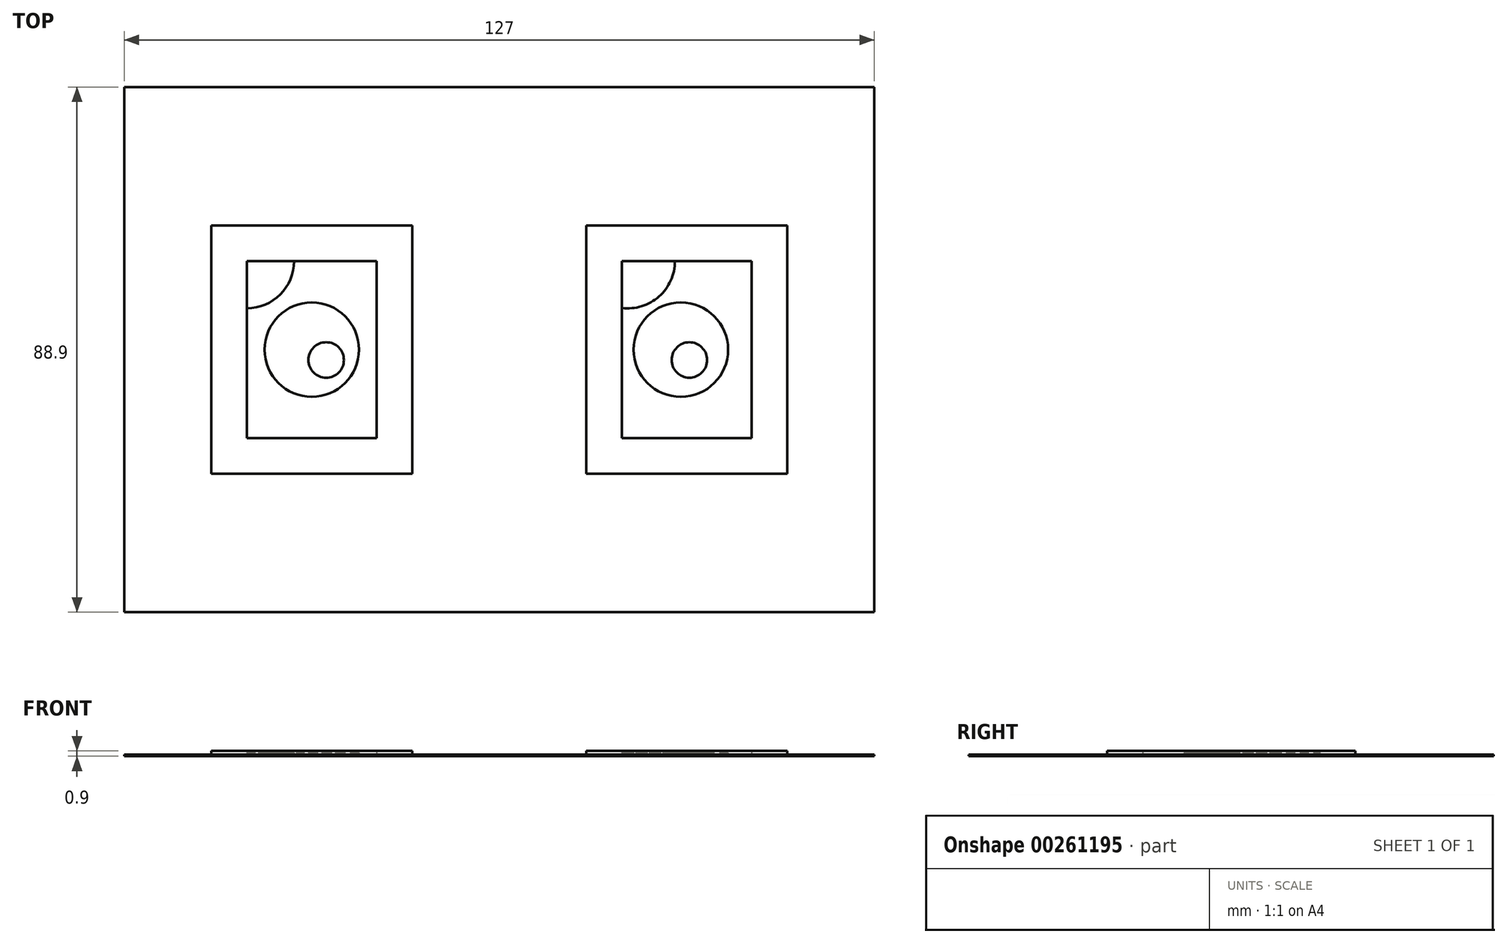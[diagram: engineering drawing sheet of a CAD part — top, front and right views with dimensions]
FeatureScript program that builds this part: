
annotation { "Feature Type Name" : "Feature", "Feature Type Description" : "" }
export const myFeature = defineFeature(function(context is Context, id is Id, definition is map)
    precondition{}
    {
        {
            var Q0;
            Q0=qCreatedBy(makeId("Top.planeOp"),FACE);
            var sketch = newSketch(context, id + "F0", { "sketchPlane" : qUnion([Q0])});
            skLineSegment(sketch, "E0.bottom", {"start": v(63.5, -44.45) * mm, "end": v(-63.5, -44.45) * mm});
            skLineSegment(sketch, "E0.top", {"start": v(63.5, 44.45) * mm, "end": v(-63.5, 44.45) * mm});
            skLineSegment(sketch, "E0.left", {"start": v(63.5, -44.45) * mm, "end": v(63.5, 44.45) * mm});
            skLineSegment(sketch, "E0.right", {"start": v(-63.5, -44.45) * mm, "end": v(-63.5, 44.45) * mm});
            skPoint(sketch, "E0.middle", {"position": v(0, 0) * mm});
            skSolve(sketch);
        }
        {
            var Q0;
            Q0 = qSketchRegion(id + "F0", true);
            extrude(context, id + "F1", {"entities" : qUnion([Q0]), "depth" : .3 * mm});
        }
        {
            var Q0;
            Q0=makeQuery(id+"F1.opExtrude","CAP_FACE",FACE,{"disambiguationData":[OSD([sQuery(id+"F0.wireOp",EDGE,"E0.bottom"),sQuery(id+"F0.wireOp",EDGE,"E0.top"),sQuery(id+"F0.wireOp",EDGE,"E0.left"),sQuery(id+"F0.wireOp",EDGE,"E0.right")])],"isStart":false});
            var sketch = newSketch(context, id + "F2", { "sketchPlane" : qUnion([Q0])});
            skLineSegment(sketch, "E1", {"start": v(0, 44.45) * mm, "end": v(0, -44.45) * mm, "construction": true});
            skLineSegment(sketch, "E2", {"start": v(0, -44.45) * mm, "end": v(63.5, 44.45) * mm, "construction": true});
            skLineSegment(sketch, "E3", {"start": v(-63.5, -44.45) * mm, "end": v(0, 44.45) * mm, "construction": true});
            skLineSegment(sketch, "E4", {"start": v(-31.75, 0) * mm, "end": v(31.75, 0) * mm, "construction": true});
            skLineSegment(sketch, "E5.bottom", {"start": v(-20.75, -15) * mm, "end": v(-42.75, -15) * mm});
            skLineSegment(sketch, "E5.top", {"start": v(-20.75, 15) * mm, "end": v(-42.75, 15) * mm});
            skLineSegment(sketch, "E5.left", {"start": v(-20.75, -15) * mm, "end": v(-20.75, 15) * mm});
            skLineSegment(sketch, "E5.right", {"start": v(-42.75, -15) * mm, "end": v(-42.75, 15) * mm});
            skPoint(sketch, "E5.middle", {"position": v(-31.75, 0) * mm});
            skLineSegment(sketch, "E6.0", {"start": v(-14.75, 21) * mm, "end": v(-48.75, 21) * mm});
            skLineSegment(sketch, "E6.1", {"start": v(-14.75, -21) * mm, "end": v(-14.75, 21) * mm});
            skLineSegment(sketch, "E6.2", {"start": v(-14.75, -21) * mm, "end": v(-48.75, -21) * mm});
            skLineSegment(sketch, "E6.3", {"start": v(-48.75, -21) * mm, "end": v(-48.75, 21) * mm});
            skLineSegment(sketch, "E7.1.0.0", {"start": v(42.75, 15) * mm, "end": v(20.75, 15) * mm});
            skLineSegment(sketch, "E7.1.0.1", {"start": v(48.75, 21) * mm, "end": v(14.75, 21) * mm});
            skLineSegment(sketch, "E7.1.0.2", {"start": v(14.75, -21) * mm, "end": v(14.75, 21) * mm});
            skLineSegment(sketch, "E7.1.0.3", {"start": v(20.75, -15) * mm, "end": v(20.75, 15) * mm});
            skLineSegment(sketch, "E7.1.0.4", {"start": v(48.75, -21) * mm, "end": v(14.75, -21) * mm});
            skLineSegment(sketch, "E7.1.0.5", {"start": v(42.75, -15) * mm, "end": v(20.75, -15) * mm});
            skLineSegment(sketch, "E7.1.0.6", {"start": v(42.75, -15) * mm, "end": v(42.75, 15) * mm});
            skLineSegment(sketch, "E7.1.0.7", {"start": v(48.75, -21) * mm, "end": v(48.75, 21) * mm});
            skLineSegment(sketch, "E7.direction1", {"start": v(-42.75, 15) * mm, "end": v(20.75, 15) * mm, "construction": true});
            skCircle(sketch, "E8", {"center": v(-31.75, 0) * mm, "radius": 8 * mm});
            skCircle(sketch, "E9", {"center": v(30.75, 0) * mm, "radius": 8 * mm});
            skLineSegment(sketch, "E10", {"start": v(30.75, 0) * mm, "end": v(31.75, 0) * mm, "construction": true});
            skArc(sketch, "E11", {"start": v(-42.75, 7) * mm, "mid": v(-37.1, 9.34) * mm, "end": v(-34.75, 15) * mm});
            skArc(sketch, "E12", {"start": v(20.75, 7.06) * mm, "mid": v(27.04, 9) * mm, "end": v(29.75, 15) * mm});
            skLineSegment(sketch, "E13", {"start": v(20.75, 15) * mm, "end": v(21.75, 15) * mm, "construction": true});
            skLineSegment(sketch, "E14", {"start": v(-31.75, 0) * mm, "end": v(-29.3, -1.74) * mm, "construction": true});
            skCircle(sketch, "E15", {"center": v(-29.3, -1.74) * mm, "radius": 3 * mm});
            skLineSegment(sketch, "E16", {"start": v(31.75, 0) * mm, "end": v(34.2, -1.74) * mm, "construction": true});
            skLineSegment(sketch, "E17", {"start": v(34.2, -1.74) * mm, "end": v(32.2, -1.74) * mm, "construction": true});
            skCircle(sketch, "E18", {"center": v(32.2, -1.74) * mm, "radius": 3 * mm});
            skSolve(sketch);
        }
        {
            var Q0;
            Q0=makeQuery(id+"F2.imprint","IMPRINT",FACE,{"disambiguationData":[TD([[makeQuery(id+"F2.imprint","IMPRINT",EDGE,{"derivedFrom":sQuery(id+"F2.wireOp",EDGE,"E8")}),1.0]])]});
            var Q1;
            Q1=makeQuery(id+"F2.imprint","IMPRINT",FACE,{"disambiguationData":[TD([[makeQuery(id+"F2.imprint","IMPRINT",EDGE,{"derivedFrom":sQuery(id+"F2.wireOp",EDGE,"E9")}),1.0]])]});
            var Q2;
            {var subQ3=sQuery(id+"F2.wireOp",EDGE,"E11");Q2=makeQuery(id+"F2.imprint","IMPRINT",FACE,{"disambiguationData":[TD([[makeQuery(id+"F2.imprint","IMPRINT",EDGE,{"derivedFrom":subQ3}),1.0]])]});}
            var Q3;
            {var subQ3=sQuery(id+"F2.wireOp",EDGE,"E12");Q3=makeQuery(id+"F2.imprint","IMPRINT",FACE,{"disambiguationData":[TD([[makeQuery(id+"F2.imprint","IMPRINT",EDGE,{"derivedFrom":subQ3}),1.0]])]});}
            var Q4;
            Q4=makeQuery(id+"F2.imprint","IMPRINT",FACE,{"disambiguationData":[TD([[makeQuery(id+"F2.imprint","IMPRINT",EDGE,{"derivedFrom":sQuery(id+"F2.wireOp",EDGE,"E15")}),1.0]])]});
            var Q5;
            Q5=makeQuery(id+"F2.imprint","IMPRINT",FACE,{"disambiguationData":[TD([[makeQuery(id+"F2.imprint","IMPRINT",EDGE,{"derivedFrom":sQuery(id+"F2.wireOp",EDGE,"E18")}),1.0]])]});
            extrude(context, id + "F3", {"entities" : qUnion([Q0, Q1, Q2, Q3, Q4, Q5]), "operationType" : NewBodyOperationType.ADD, "depth" : .3 * mm});
        }
        {
            var Q0;
            Q0=makeQuery(id+"F2.imprint","IMPRINT",FACE,{"disambiguationData":[TD([[makeQuery(id+"F2.imprint","IMPRINT",EDGE,{"derivedFrom":sQuery(id+"F2.wireOp",EDGE,"E15")}),1.0]])]});
            var Q1;
            Q1=makeQuery(id+"F2.imprint","IMPRINT",FACE,{"disambiguationData":[TD([[makeQuery(id+"F2.imprint","IMPRINT",EDGE,{"derivedFrom":sQuery(id+"F2.wireOp",EDGE,"E18")}),1.0]])]});
            var Q2;
            {var subQ6=sQuery(id+"F2.wireOp",EDGE,"E5.bottom");Q2=makeQuery(id+"F2.imprint","IMPRINT",FACE,{"disambiguationData":[TD([[makeQuery(id+"F2.imprint","IMPRINT",EDGE,{"derivedFrom":subQ6}),1.0]])]});}
            var Q3;
            Q3=makeQuery(id+"F2.imprint","IMPRINT",FACE,{"disambiguationData":[TD([[makeQuery(id+"F2.imprint","IMPRINT",EDGE,{"derivedFrom":sQuery(id+"F2.wireOp",EDGE,"E7.1.0.1")}),1.0]])]});
            extrude(context, id + "F4", {"entities" : qUnion([Q0, Q1, Q2, Q3]), "operationType" : NewBodyOperationType.ADD, "depth" : .6 * mm});
        }
    });
